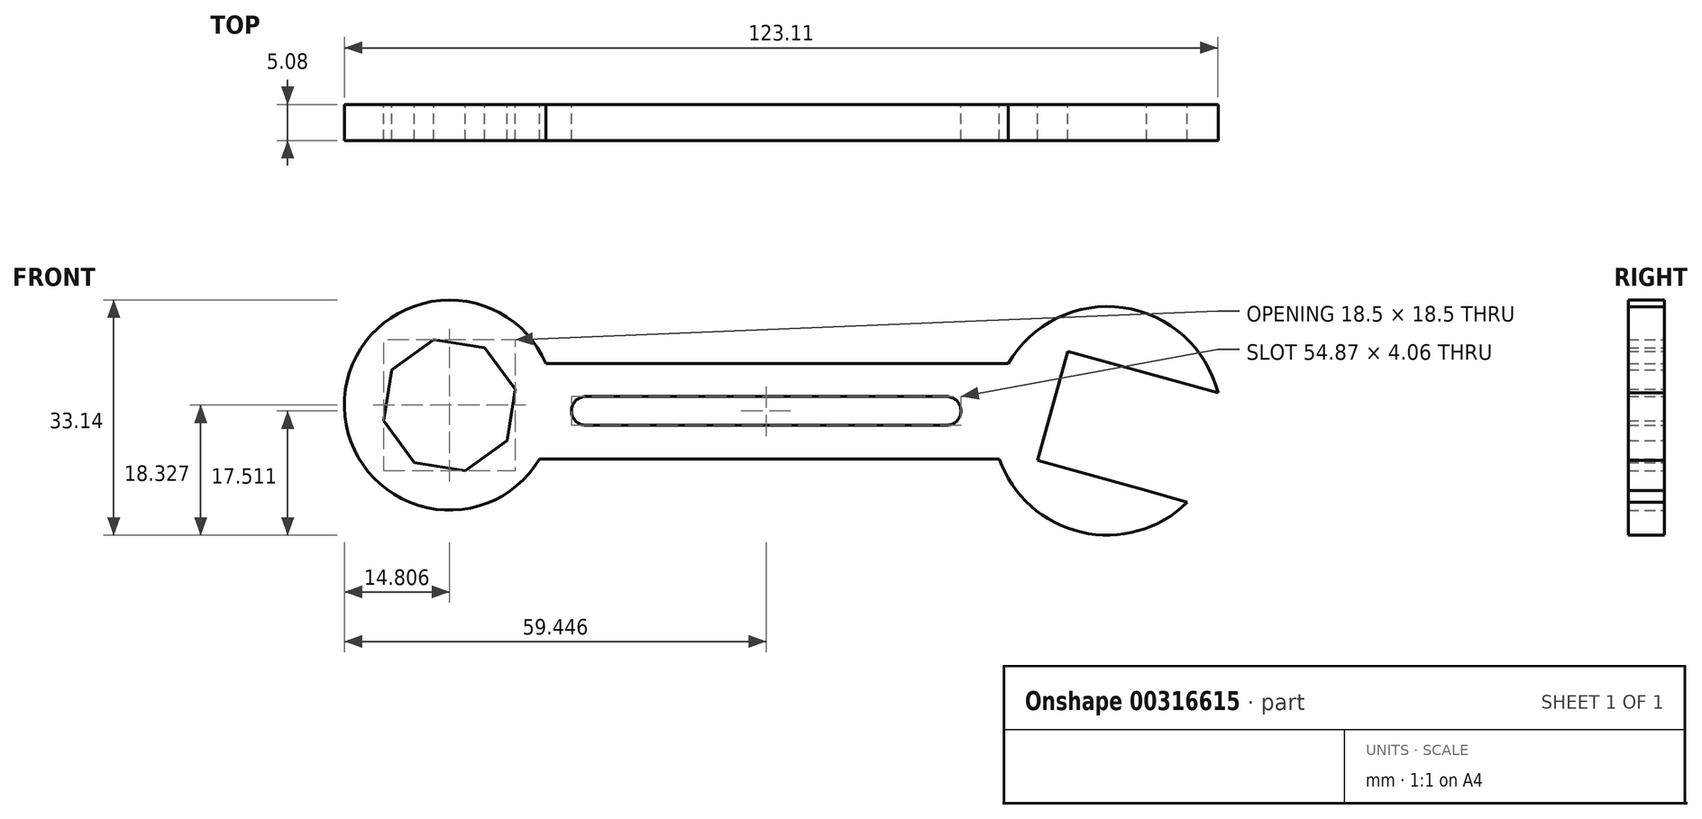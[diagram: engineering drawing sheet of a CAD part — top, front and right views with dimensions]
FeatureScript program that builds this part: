
annotation { "Feature Type Name" : "Feature", "Feature Type Description" : "" }
export const myFeature = defineFeature(function(context is Context, id is Id, definition is map)
    precondition{}
    {
        {
            var Q0;
            Q0=qCreatedBy(makeId("Front.planeOp"),FACE);
            var sketch = newSketch(context, id + "F0", { "sketchPlane" : qUnion([Q0])});
            skCircle(sketch, "E0.cCircle", {"center": v(-47.91, 15.45) * mm, "radius": 9.51 * mm, "construction": true});
            skLineSegment(sketch, "E0.0", {"start": v(-38.66, 17.67) * mm, "end": v(-39.8, 10.48) * mm});
            skLineSegment(sketch, "E0.1", {"start": v(-39.8, 10.48) * mm, "end": v(-45.7, 6.2) * mm});
            skLineSegment(sketch, "E0.2", {"start": v(-45.7, 6.2) * mm, "end": v(-52.88, 7.34) * mm});
            skLineSegment(sketch, "E0.3", {"start": v(-52.88, 7.34) * mm, "end": v(-57.16, 13.23) * mm});
            skLineSegment(sketch, "E0.4", {"start": v(-57.16, 13.23) * mm, "end": v(-56.02, 20.42) * mm});
            skLineSegment(sketch, "E0.5", {"start": v(-56.02, 20.42) * mm, "end": v(-50.13, 24.7) * mm});
            skLineSegment(sketch, "E0.6", {"start": v(-50.13, 24.7) * mm, "end": v(-42.94, 23.56) * mm});
            skLineSegment(sketch, "E0.7", {"start": v(-42.94, 23.56) * mm, "end": v(-38.66, 17.67) * mm});
            skArc(sketch, "E1", {"start": v(-34.31, 21.31) * mm, "mid": v(-62.72, 15.45) * mm, "end": v(-34.31, 9.58) * mm});
            skLineSegment(sketch, "E2.bottom", {"start": v(-34.31, 21.31) * mm, "end": v(30.83, 21.31) * mm});
            skLineSegment(sketch, "E2.top", {"start": v(-34.31, 7.86) * mm, "end": v(29.58, 7.86) * mm});
            skLineSegment(sketch, "E2.left", {"start": v(-34.31, 21.31) * mm, "end": v(-34.31, 9.58) * mm});
            skLineSegment(sketch, "E2.right", {"start": v(38.66, 21.31) * mm, "end": v(38.66, 21.03) * mm});
            skArc(sketch, "E3", {"start": v(60.4, 17.16) * mm, "mid": v(29.26, 17.59) * mm, "end": v(56.05, 1.73) * mm});
            skLineSegment(sketch, "E4.1", {"start": v(50.32, 3.42) * mm, "end": v(34.96, 7.68) * mm});
            skLineSegment(sketch, "E4.2", {"start": v(34.96, 7.68) * mm, "end": v(39.22, 23.03) * mm});
            skLineSegment(sketch, "E4.3", {"start": v(39.22, 23.03) * mm, "end": v(54.57, 18.78) * mm});
            skLineSegment(sketch, "E5", {"start": v(50.32, 3.42) * mm, "end": v(56.05, 1.73) * mm});
            skLineSegment(sketch, "E6", {"start": v(-34.31, 7.86) * mm, "end": v(-35.2, 7.86) * mm});
            skLineSegment(sketch, "E7", {"start": v(39.22, 23.03) * mm, "end": v(60.4, 17.16) * mm});
            skLineSegment(sketch, "E8", {"start": v(-28.68, 16.66) * mm, "end": v(22.13, 16.66) * mm});
            skLineSegment(sketch, "E9", {"start": v(-28.68, 12.6) * mm, "end": v(22.13, 12.6) * mm});
            skArc(sketch, "E10", {"start": v(22.13, 12.6) * mm, "mid": v(24.16, 14.63) * mm, "end": v(22.13, 16.66) * mm});
            skArc(sketch, "E11", {"start": v(-28.68, 16.66) * mm, "mid": v(-30.7, 14.63) * mm, "end": v(-28.68, 12.6) * mm});
            skSolve(sketch);
        }
        {
            var Q0;
            Q0=makeQuery(id+"F0.imprint","IMPRINT",FACE,{"disambiguationData":[TD([[makeQuery(id+"F0.imprint","IMPRINT",EDGE,{"derivedFrom":sQuery(id+"F0.wireOp",EDGE,"E0.0")}),1.0]])]});
            var Q1;
            {var subQ4=sQuery(id+"F0.wireOp",EDGE,"E2.bottom");Q1=makeQuery(id+"F0.imprint","IMPRINT",FACE,{"disambiguationData":[TD([[makeQuery(id+"F0.imprint","IMPRINT",EDGE,{"derivedFrom":subQ4}),-1.0]])]});}
            var Q2;
            {var subQ3=sQuery(id+"F0.wireOp",EDGE,"E4.1");Q2=makeQuery(id+"F0.imprint","IMPRINT",FACE,{"disambiguationData":[TD([[makeQuery(id+"F0.imprint","IMPRINT",EDGE,{"derivedFrom":subQ3}),1.0]])]});}
            var Q3;
            {var subQ4=sQuery(id+"F0.wireOp",EDGE,"E2.left");Q3=makeQuery(id+"F0.imprint","IMPRINT",FACE,{"disambiguationData":[TD([[makeQuery(id+"F0.imprint","IMPRINT",EDGE,{"derivedFrom":subQ4}),1.0]])]});}
            var Q4;
            {var subQ1=sQuery(id+"F0.wireOp",EDGE,"E2.right");Q4=makeQuery(id+"F0.imprint","IMPRINT",FACE,{"disambiguationData":[TD([[makeQuery(id+"F0.imprint","IMPRINT",EDGE,{"derivedFrom":subQ1}),1.0]])]});}
            extrude(context, id + "F1", {"entities" : qUnion([Q0, Q1, Q2, Q3, Q4]), "endBound" : BoundingType.SYMMETRIC, "depth" : 5.08 * mm});
        }
    });
